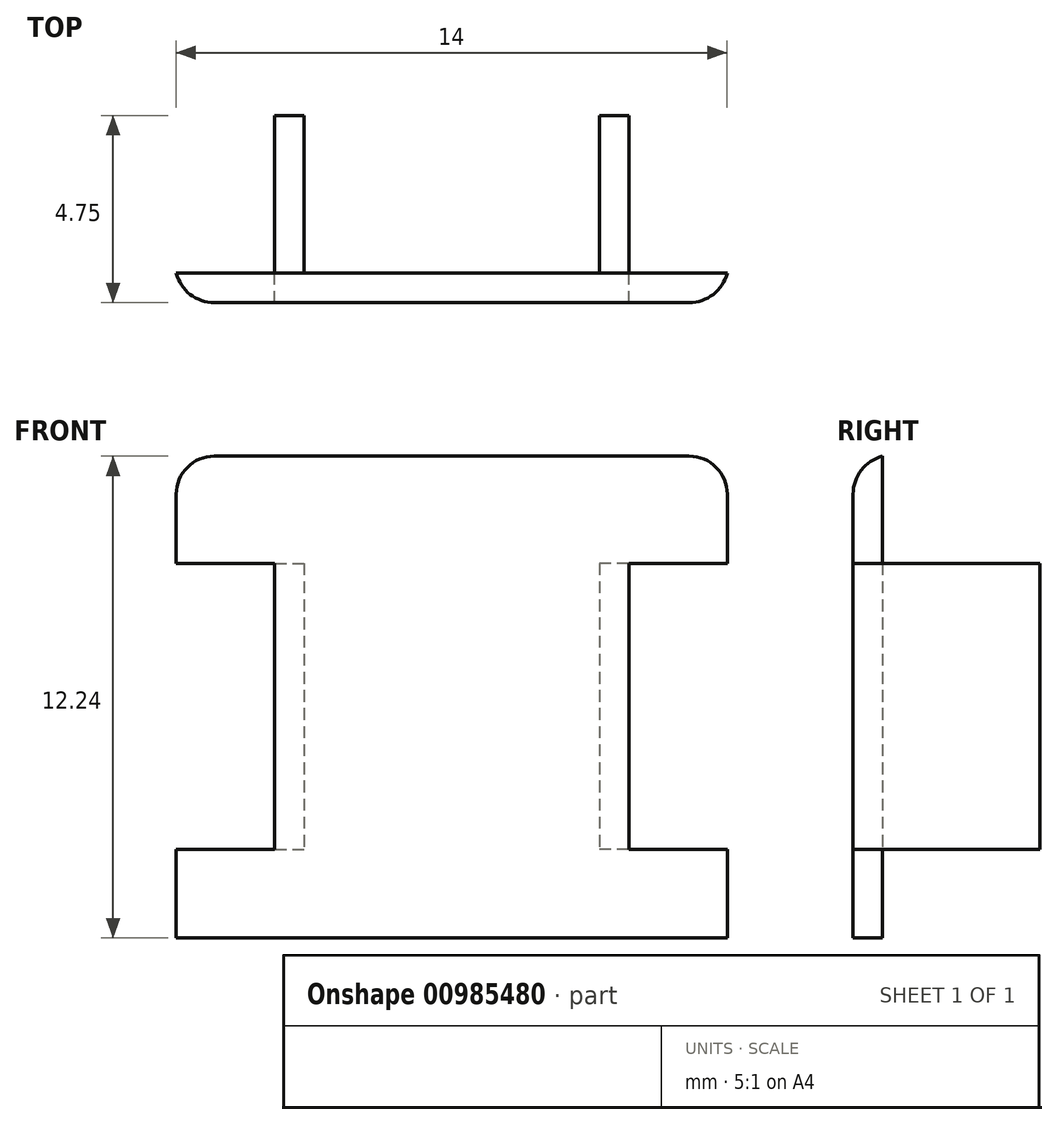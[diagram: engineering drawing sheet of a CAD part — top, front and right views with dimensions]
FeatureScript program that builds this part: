
annotation { "Feature Type Name" : "Feature", "Feature Type Description" : "" }
export const myFeature = defineFeature(function(context is Context, id is Id, definition is map)
    precondition{}
    {
        {
            var Q0;
            Q0=qCreatedBy(makeId("Top.planeOp"),FACE);
            var sketch = newSketch(context, id + "F0", { "sketchPlane" : qUnion([Q0])});
            skLineSegment(sketch, "E0", {"start": v(-12.42, 3.7) * mm, "end": v(1.58, 3.7) * mm});
            skArc(sketch, "E1", {"start": v(-12.42, 3.7) * mm, "mid": v(-12.06, 3.16) * mm, "end": v(-11.45, 2.95) * mm});
            skArc(sketch, "E2", {"start": v(0.61, 2.95) * mm, "mid": v(1.23, 3.16) * mm, "end": v(1.58, 3.7) * mm});
            skLineSegment(sketch, "E3", {"start": v(-11.45, 2.95) * mm, "end": v(0.61, 2.95) * mm});
            skSolve(sketch);
        }
        {
            var Q0;
            Q0=qSketchRegion(id+"F0",true);
            extrude(context, id + "F1", {"entities" : qUnion([Q0]), "depth" : (10 + 2.27) * mm});
        }
        {
            var Q0;
            Q0=makeQuery(id+"F1.opExtrude","CAP_EDGE",EDGE,{"disambiguationData":[OSD([sQuery(id+"F0.wireOp",EDGE,"E3")])],"isStart":false});
            fillet(context, id + "F2", {"entities" : qUnion([Q0]), "radius" : 1 * mm, "tangentPropagation" : true, "allowEdgeOverflow" : false});
        }
        {
            var Q0;
            Q0=makeQuery(id+"F1.opExtrude","SWEPT_FACE",FACE,{"disambiguationData":[OSD([sQuery(id+"F0.wireOp",EDGE,"E0")])]});
            var sketch = newSketch(context, id + "F3", { "sketchPlane" : qUnion([Q0])});
            skLineSegment(sketch, "E4.bottom", {"start": v(12.42, 9.52) * mm, "end": v(9.92, 9.52) * mm});
            skLineSegment(sketch, "E4.top", {"start": v(12.42, 2.25) * mm, "end": v(9.92, 2.25) * mm});
            skLineSegment(sketch, "E4.left", {"start": v(12.42, 9.52) * mm, "end": v(12.42, 2.25) * mm});
            skLineSegment(sketch, "E4.right", {"start": v(9.92, 9.52) * mm, "end": v(9.92, 2.25) * mm});
            skLineSegment(sketch, "E5", {"start": v(5.42, 12.24) * mm, "end": v(5.42, 0) * mm, "construction": true});
            skLineSegment(sketch, "E6.MirrorCS", {"start": v(0.92, 9.52) * mm, "end": v(0.92, 2.25) * mm});
            skLineSegment(sketch, "E7.MirrorCS", {"start": v(-1.58, 9.52) * mm, "end": v(-1.58, 2.25) * mm});
            skLineSegment(sketch, "E8.MirrorCS", {"start": v(-1.58, 2.25) * mm, "end": v(0.92, 2.25) * mm});
            skLineSegment(sketch, "E9.MirrorCS", {"start": v(-1.58, 9.52) * mm, "end": v(0.92, 9.52) * mm});
            skSolve(sketch);
        }
        {
            var Q0;
            Q0=qSketchRegion(id+"F3",true);
            extrude(context, id + "F4", {"entities" : qUnion([Q0]), "operationType" : NewBodyOperationType.REMOVE, "endBound" : BoundingType.THROUGH_ALL, "oppositeDirection" : true, "depth" : 25 * mm});
        }
        {
            var Q0;
            Q0=makeQuery(id+"F1.opExtrude","SWEPT_FACE",FACE,{"disambiguationData":[OSD([sQuery(id+"F0.wireOp",EDGE,"E0")])]});
            var sketch = newSketch(context, id + "F5", { "sketchPlane" : qUnion([Q0])});
            skLineSegment(sketch, "E10.bottom", {"start": v(0.92, 9.52) * mm, "end": v(1.67, 9.52) * mm});
            skLineSegment(sketch, "E10.top", {"start": v(0.92, 2.25) * mm, "end": v(1.67, 2.25) * mm});
            skLineSegment(sketch, "E10.left", {"start": v(0.92, 9.52) * mm, "end": v(0.92, 2.25) * mm});
            skLineSegment(sketch, "E10.right", {"start": v(1.67, 9.52) * mm, "end": v(1.67, 2.25) * mm});
            skLineSegment(sketch, "E11", {"start": v(5.42, 12.24) * mm, "end": v(5.42, 0) * mm, "construction": true});
            skLineSegment(sketch, "E12.MirrorCS", {"start": v(9.92, 9.52) * mm, "end": v(9.17, 9.52) * mm});
            skLineSegment(sketch, "E13.MirrorCS", {"start": v(9.17, 9.52) * mm, "end": v(9.17, 2.25) * mm});
            skLineSegment(sketch, "E14.MirrorCS", {"start": v(9.92, 9.52) * mm, "end": v(9.92, 2.25) * mm});
            skLineSegment(sketch, "E15.MirrorCS", {"start": v(9.92, 2.25) * mm, "end": v(9.17, 2.25) * mm});
            skSolve(sketch);
        }
        {
            var Q0;
            Q0=qSketchRegion(id+"F5",true);
            extrude(context, id + "F6", {"entities" : qUnion([Q0]), "operationType" : NewBodyOperationType.ADD, "depth" : 4 * mm});
        }
    });
